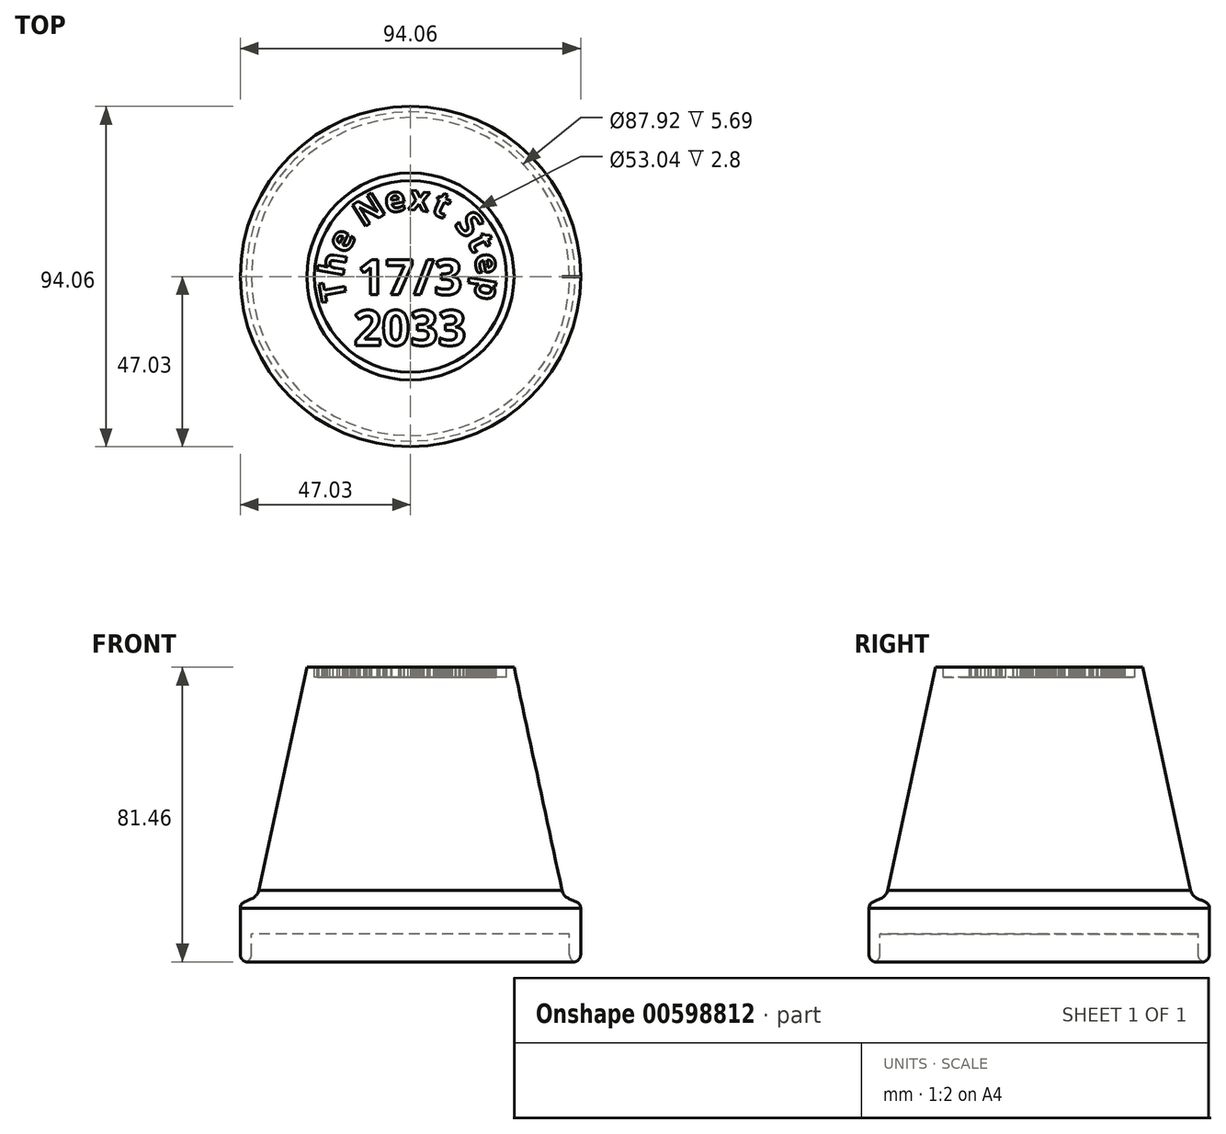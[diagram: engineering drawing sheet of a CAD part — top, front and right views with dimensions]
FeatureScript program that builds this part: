
annotation { "Feature Type Name" : "Feature", "Feature Type Description" : "" }
export const myFeature = defineFeature(function(context is Context, id is Id, definition is map)
    precondition{}
    {
        {
            var Q0;
            Q0=qCreatedBy(makeId("Front.planeOp"),FACE);
            var sketch = newSketch(context, id + "F0", { "sketchPlane" : qUnion([Q0])});
            skLineSegment(sketch, "E0", {"start": v(20.44, 0) * mm, "end": v(0, 0) * mm});
            skLineSegment(sketch, "E1.MirrorCS", {"start": v(32.1, -58.24) * mm, "end": v(32.9, -58.24) * mm});
            skArc(sketch, "E2.MirrorCS", {"start": v(32.9, -58.24) * mm, "mid": v(31.84, -57.8) * mm, "end": v(31.4, -56.74) * mm});
            skArc(sketch, "E3.MirrorCS", {"start": v(33.6, -56.74) * mm, "mid": v(33.16, -57.8) * mm, "end": v(32.1, -58.24) * mm});
            skFitSpline(sketch, "E4.MirrorCS", {"points": [v(29.93, -44.04) * mm, v(33.6, -47.6) * mm], "startDerivative": vector(1.58, -7.33) * mm, "endDerivative": vector(0, -6) * mm});
            skLineSegment(sketch, "E5.MirrorCS", {"start": v(31.4, -52.68) * mm, "end": v(31.4, -56.74) * mm});
            skLineSegment(sketch, "E6.MirrorCS", {"start": v(20.44, 0) * mm, "end": v(29.93, -44.04) * mm});
            skLineSegment(sketch, "E7.MirrorCS", {"start": v(33.6, -56.74) * mm, "end": v(33.6, -47.6) * mm});
            skPoint(sketch, "E8.MirrorP", {"position": v(33.6, -58.24) * mm});
            skLineSegment(sketch, "E9.MirrorCS", {"start": v(0, 0) * mm, "end": v(0, -52.68) * mm});
            skLineSegment(sketch, "E10.MirrorCS", {"start": v(0, -52.68) * mm, "end": v(31.4, -52.68) * mm});
            skPoint(sketch, "E11.MirrorP", {"position": v(31.4, -58.24) * mm});
            skFitSpline(sketch, "E12.MirrorCS", {"points": [v(29.93, -44.04) * mm, v(33.6, -47.6) * mm], "startDerivative": vector(1.58, -7.33) * mm, "endDerivative": vector(0, -6) * mm});
            skFitSpline(sketch, "E13.MirrorCS", {"points": [v(29.93, -44.04) * mm, v(33.6, -47.6) * mm], "startDerivative": vector(1.58, -7.33) * mm, "endDerivative": vector(0, -6) * mm});
            skSolve(sketch);
        }
        {
            var Q0;
            Q0=makeQuery(id+"F0.imprint","IMPRINT",FACE,{"disambiguationData":[TD([[makeQuery(id+"F0.imprint","IMPRINT",EDGE,{"derivedFrom":sQuery(id+"F0.wireOp",EDGE,"E0")}),1.0]])]});
            var Q1;
            Q1=sQuery(id+"F0.wireOp",EDGE,"E9.MirrorCS");
            revolve(context, id + "F1", {"entities" : qUnion([Q0]), "axis" : qUnion([Q1]), "revolveType" : RevolveType.FULL});
        }
        {
            var Q0;
            Q0=qCreatedBy(makeId("Top.planeOp"),FACE);
            var sketch = newSketch(context, id + "F2", { "sketchPlane" : qUnion([Q0])});
            skText(sketch, "E14", { "text": "T", "fontName": "OpenSans-Bold.ttf"});
            skText(sketch, "E15", { "text": "h", "fontName": "OpenSans-Bold.ttf"});
            skText(sketch, "E16", { "text": "e", "fontName": "OpenSans-Bold.ttf"});
            skText(sketch, "E17", { "text": "N", "fontName": "OpenSans-Bold.ttf"});
            skText(sketch, "E18", { "text": "e", "fontName": "OpenSans-Bold.ttf"});
            skText(sketch, "E19", { "text": "x", "fontName": "OpenSans-Bold.ttf"});
            skText(sketch, "E20", { "text": "t", "fontName": "OpenSans-Bold.ttf"});
            skText(sketch, "E21", { "text": "S", "fontName": "OpenSans-Bold.ttf"});
            skText(sketch, "E22", { "text": "t", "fontName": "OpenSans-Bold.ttf"});
            skText(sketch, "E23", { "text": "e", "fontName": "OpenSans-Bold.ttf"});
            skText(sketch, "E24", { "text": "p", "fontName": "OpenSans-Bold.ttf"});
            skCircle(sketch, "E25", {"center": v(0, 0) * mm, "radius": 13.1 * mm, "construction": true});
            skLineSegment(sketch, "E26", {"start": v(-13.1, -0.17) * mm, "end": v(-8.65, -0.1) * mm, "construction": true});
            skLineSegment(sketch, "E27", {"start": v(-8.2, 2.78) * mm, "end": v(-12.41, 4.2) * mm, "construction": true});
            skLineSegment(sketch, "E28", {"start": v(-10.45, 7.92) * mm, "end": v(-6.9, 5.23) * mm, "construction": true});
            skLineSegment(sketch, "E29", {"start": v(-10.45, 7.92) * mm, "end": v(-9.12, 9.42) * mm});
            skLineSegment(sketch, "E30", {"start": v(-9.12, 9.42) * mm, "end": v(-6.02, 6.22) * mm, "construction": true});
            skLineSegment(sketch, "E31", {"start": v(-4.6, 12.28) * mm, "end": v(-3.03, 8.1) * mm, "construction": true});
            skLineSegment(sketch, "E32", {"start": v(-0.47, 13.1) * mm, "end": v(-0.31, 8.65) * mm, "construction": true});
            skLineSegment(sketch, "E33", {"start": v(3.86, 12.53) * mm, "end": v(2.55, 8.27) * mm, "construction": true});
            skLineSegment(sketch, "E34", {"start": v(6.8, 11.21) * mm, "end": v(4.48, 7.4) * mm, "construction": true});
            skLineSegment(sketch, "E35", {"start": v(11.03, 7.08) * mm, "end": v(7.28, 4.67) * mm, "construction": true});
            skLineSegment(sketch, "E36", {"start": v(12.42, 4.18) * mm, "end": v(8.2, 2.76) * mm, "construction": true});
            skLineSegment(sketch, "E37", {"start": v(8.42, 10.05) * mm, "end": v(5.56, 6.63) * mm, "construction": true});
            skLineSegment(sketch, "E38", {"start": v(13.1, 0.04) * mm, "end": v(8.65, 0.02) * mm, "construction": true});
            skText(sketch, "E39", { "text": "17/3", "fontName": "OpenSans-Bold.ttf"});
            skText(sketch, "E40", { "text": "2033", "fontName": "OpenSans-Bold.ttf"});
            skLineSegment(sketch, "E41", {"start": v(-12.52, -4.43) * mm, "end": v(12.54, -4.43) * mm, "construction": true});
            skCircle(sketch, "E42", {"center": v(0, 0) * mm, "radius": 18.94 * mm});
            const initialGuessF2  = {"E14": [-0.01252, -0.00443, -0.17546, 0.98449, 0.005], "E15": [-0.0133, -0.00017, 0.15646, 0.98768, 0.005], "E16": [-0.01258, 0.00426, 0.46859, 0.88342, 0.005], "E17": [-0.00932, 0.00962, 0.84527, 0.53435, 0.005], "E18": [-0.00465, 0.01244, 0.98064, 0.19581, 0.005], "E19": [-0.00048, 0.01329, 0.9914, -0.13087, 0.005], "E20": [0.00389, 0.01262, 0.9124, -0.4093, 0.005], "E21": [0.00852, 0.01016, 0.66084, -0.75052, 0.005], "E22": [0.01112, 0.00713, 0.43272, -0.90153, 0.005], "E23": [0.01259, 0.00423, 0.1629, -0.98664, 0.005], "E24": [0.0133, 4e-05, -0.16769, -0.98584, 0.005], "E39": [-0.01046, -0.0036, 1, 0, 0.007], "E40": [-0.01123, -0.01363, 1, 0, 0.007]};
            skSetInitialGuess(sketch, initialGuessF2);
            skSolve(sketch);
        }
        {
            var Q0;
            Q0=makeQuery(id+"F2.imprint","IMPRINT",FACE,{"disambiguationData":[TD([[makeQuery(id+"F2.imprint","IMPRINT",EDGE,{"derivedFrom":sQuery(id+"F2.wireOp",EDGE,"E16.sketch_text.stroke-0")}),1.0]])]});
            var Q1;
            Q1=makeQuery(id+"F2.imprint","IMPRINT",FACE,{"disambiguationData":[TD([[makeQuery(id+"F2.imprint","IMPRINT",EDGE,{"derivedFrom":sQuery(id+"F2.wireOp",EDGE,"E18.sketch_text.stroke-0")}),1.0]])]});
            var Q2;
            Q2=makeQuery(id+"F2.imprint","IMPRINT",FACE,{"disambiguationData":[TD([[makeQuery(id+"F2.imprint","IMPRINT",EDGE,{"derivedFrom":sQuery(id+"F2.wireOp",EDGE,"E23.sketch_text.stroke-0")}),1.0]])]});
            var Q3;
            Q3=makeQuery(id+"F2.imprint","IMPRINT",FACE,{"disambiguationData":[TD([[makeQuery(id+"F2.imprint","IMPRINT",EDGE,{"derivedFrom":sQuery(id+"F2.wireOp",EDGE,"E24.sketch_text.stroke-15")}),1.0]])]});
            var Q4;
            Q4=makeQuery(id+"F2.imprint","IMPRINT",FACE,{"disambiguationData":[TD([[makeQuery(id+"F2.imprint","IMPRINT",EDGE,{"derivedFrom":sQuery(id+"F2.wireOp",EDGE,"E40.sketch_text.stroke-32")}),1.0]])]});
            var Q5;
            Q5=makeQuery(id+"F2.imprint","IMPRINT",FACE,{"disambiguationData":[TD([[makeQuery(id+"F2.imprint","IMPRINT",EDGE,{"derivedFrom":sQuery(id+"F2.wireOp",EDGE,"E14.sketch_text.stroke-0")}),1.0]])]});
            var Q6;
            Q6=sQuery(id+"F2.wireOp",EDGE,"E42");
            extrude(context, id + "F3", {"entities" : qUnion([Q0, Q1, Q2, Q3, Q4, Q5]), "operationType" : NewBodyOperationType.REMOVE, "surfaceEntities" : qUnion([Q6]), "oppositeDirection" : true, "depth" : 2 * mm, "offsetDistance" : 25 * mm});
        }
        {
            var Q0;
            Q0=makeQuery(id+"F1.opRevolve","SWEPT_BODY",BODY,{"disambiguationData":[OSD([sQuery(id+"F0.wireOp",EDGE,"E0"),sQuery(id+"F0.wireOp",EDGE,"E13.MirrorCS"),sQuery(id+"F0.wireOp",EDGE,"E3.MirrorCS"),sQuery(id+"F0.wireOp",EDGE,"E2.MirrorCS"),sQuery(id+"F0.wireOp",EDGE,"E7.MirrorCS"),sQuery(id+"F0.wireOp",EDGE,"E5.MirrorCS"),sQuery(id+"F0.wireOp",EDGE,"E6.MirrorCS"),sQuery(id+"F0.wireOp",EDGE,"E10.MirrorCS"),sQuery(id+"F0.wireOp",EDGE,"E9.MirrorCS")])]});
            var Q1;
            Q1=qCreatedBy(makeId("Origin.pointOp"),VERTEX);
            transform(context, id + "F4", {"entities" : qUnion([Q0]), "transformType" : TransformType.SCALE_UNIFORMLY, "scale" : 1.4, "scalePoint" : qUnion([Q1]), "makeCopy" : false});
        }
    });
